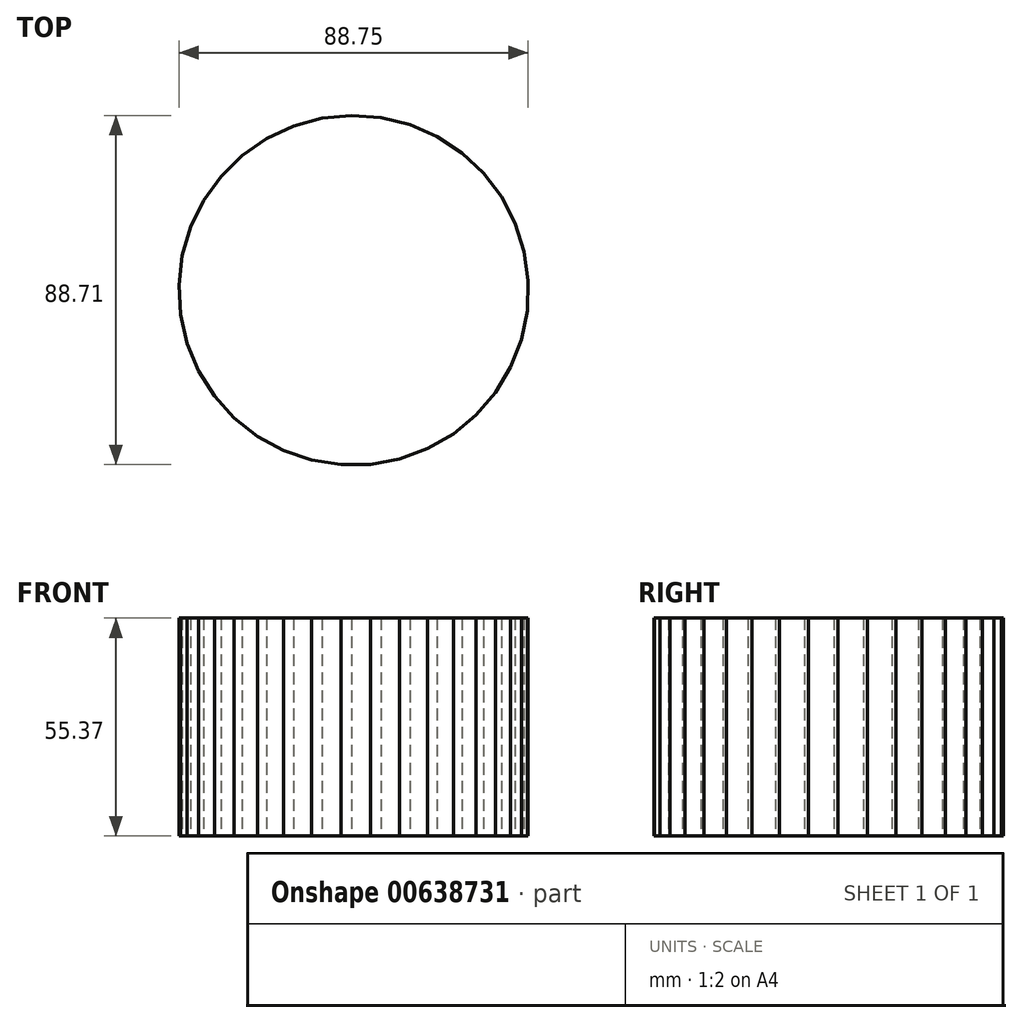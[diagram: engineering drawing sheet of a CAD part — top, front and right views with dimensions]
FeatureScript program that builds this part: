
annotation { "Feature Type Name" : "Feature", "Feature Type Description" : "" }
export const myFeature = defineFeature(function(context is Context, id is Id, definition is map)
    precondition{}
    {
        {
            var Q0;
            Q0=qCreatedBy(makeId("Top.planeOp"),FACE);
            var sketch = newSketch(context, id + "F0", { "sketchPlane" : qUnion([Q0])});
            skCircle(sketch, "E0.cCircle", {"center": v(0, 0) * mm, "radius": 44.26 * mm, "construction": true});
            skLineSegment(sketch, "E0.0", {"start": v(42.63, -12.49) * mm, "end": v(39.9, -19.51) * mm});
            skLineSegment(sketch, "E0.1", {"start": v(39.9, -19.51) * mm, "end": v(36.03, -25.97) * mm});
            skLineSegment(sketch, "E0.2", {"start": v(36.03, -25.97) * mm, "end": v(31.12, -31.7) * mm});
            skLineSegment(sketch, "E0.3", {"start": v(31.12, -31.7) * mm, "end": v(25.32, -36.5) * mm});
            skLineSegment(sketch, "E0.4", {"start": v(25.32, -36.5) * mm, "end": v(18.79, -40.25) * mm});
            skLineSegment(sketch, "E0.5", {"start": v(18.79, -40.25) * mm, "end": v(11.72, -42.84) * mm});
            skLineSegment(sketch, "E0.6", {"start": v(11.72, -42.84) * mm, "end": v(4.3, -44.2) * mm});
            skLineSegment(sketch, "E0.7", {"start": v(4.3, -44.2) * mm, "end": v(-3.23, -44.3) * mm});
            skLineSegment(sketch, "E0.8", {"start": v(-3.23, -44.3) * mm, "end": v(-10.67, -43.12) * mm});
            skLineSegment(sketch, "E0.9", {"start": v(-10.67, -43.12) * mm, "end": v(-17.8, -40.7) * mm});
            skLineSegment(sketch, "E0.10", {"start": v(-17.8, -40.7) * mm, "end": v(-24.42, -37.1) * mm});
            skLineSegment(sketch, "E0.11", {"start": v(-24.42, -37.1) * mm, "end": v(-30.34, -32.44) * mm});
            skLineSegment(sketch, "E0.12", {"start": v(-30.34, -32.44) * mm, "end": v(-35.39, -26.85) * mm});
            skLineSegment(sketch, "E0.13", {"start": v(-35.39, -26.85) * mm, "end": v(-39.42, -20.48) * mm});
            skLineSegment(sketch, "E0.14", {"start": v(-39.42, -20.48) * mm, "end": v(-42.3, -13.52) * mm});
            skLineSegment(sketch, "E0.15", {"start": v(-42.3, -13.52) * mm, "end": v(-43.99, -6.18) * mm});
            skLineSegment(sketch, "E0.16", {"start": v(-43.99, -6.18) * mm, "end": v(-44.4, 1.34) * mm});
            skLineSegment(sketch, "E0.17", {"start": v(-44.4, 1.34) * mm, "end": v(-43.53, 8.83) * mm});
            skLineSegment(sketch, "E0.18", {"start": v(-43.53, 8.83) * mm, "end": v(-41.41, 16.06) * mm});
            skLineSegment(sketch, "E0.19", {"start": v(-41.41, 16.06) * mm, "end": v(-38.1, 22.83) * mm});
            skLineSegment(sketch, "E0.20", {"start": v(-38.1, 22.83) * mm, "end": v(-33.7, 28.94) * mm});
            skLineSegment(sketch, "E0.21", {"start": v(-33.7, 28.94) * mm, "end": v(-28.32, 34.22) * mm});
            skLineSegment(sketch, "E0.22", {"start": v(-28.32, 34.22) * mm, "end": v(-22.13, 38.51) * mm});
            skLineSegment(sketch, "E0.23", {"start": v(-22.13, 38.51) * mm, "end": v(-15.3, 41.7) * mm});
            skLineSegment(sketch, "E0.24", {"start": v(-15.3, 41.7) * mm, "end": v(-8.04, 43.68) * mm});
            skLineSegment(sketch, "E0.25", {"start": v(-8.04, 43.68) * mm, "end": v(-0.54, 44.41) * mm});
            skLineSegment(sketch, "E0.26", {"start": v(-0.54, 44.41) * mm, "end": v(6.97, 43.87) * mm});
            skLineSegment(sketch, "E0.27", {"start": v(6.97, 43.87) * mm, "end": v(14.29, 42.06) * mm});
            skLineSegment(sketch, "E0.28", {"start": v(14.29, 42.06) * mm, "end": v(21.19, 39.04) * mm});
            skLineSegment(sketch, "E0.29", {"start": v(21.19, 39.04) * mm, "end": v(27.48, 34.9) * mm});
            skLineSegment(sketch, "E0.30", {"start": v(27.48, 34.9) * mm, "end": v(32.98, 29.75) * mm});
            skLineSegment(sketch, "E0.31", {"start": v(32.98, 29.75) * mm, "end": v(37.54, 23.75) * mm});
            skLineSegment(sketch, "E0.32", {"start": v(37.54, 23.75) * mm, "end": v(41, 17.06) * mm});
            skLineSegment(sketch, "E0.33", {"start": v(41, 17.06) * mm, "end": v(43.3, 9.89) * mm});
            skLineSegment(sketch, "E0.34", {"start": v(43.3, 9.89) * mm, "end": v(44.35, 2.43) * mm});
            skLineSegment(sketch, "E0.35", {"start": v(44.35, 2.43) * mm, "end": v(44.12, -5.1) * mm});
            skLineSegment(sketch, "E0.36", {"start": v(44.12, -5.1) * mm, "end": v(42.63, -12.49) * mm});
            skPoint(sketch, "E0.0.midPoint", {"position": v(41.26, -16) * mm});
            skSolve(sketch);
        }
        {
            var Q0;
            Q0=makeQuery(id+"F0.imprint","IMPRINT",FACE,{"disambiguationData":[TD([[makeQuery(id+"F0.imprint","IMPRINT",EDGE,{"derivedFrom":sQuery(id+"F0.wireOp",EDGE,"E0.0")}),-1.0]])]});
            extrude(context, id + "F1", {"entities" : qUnion([Q0]), "depth" : 55.37 * mm, "offsetDistance" : 25.4 * mm});
        }
    });
